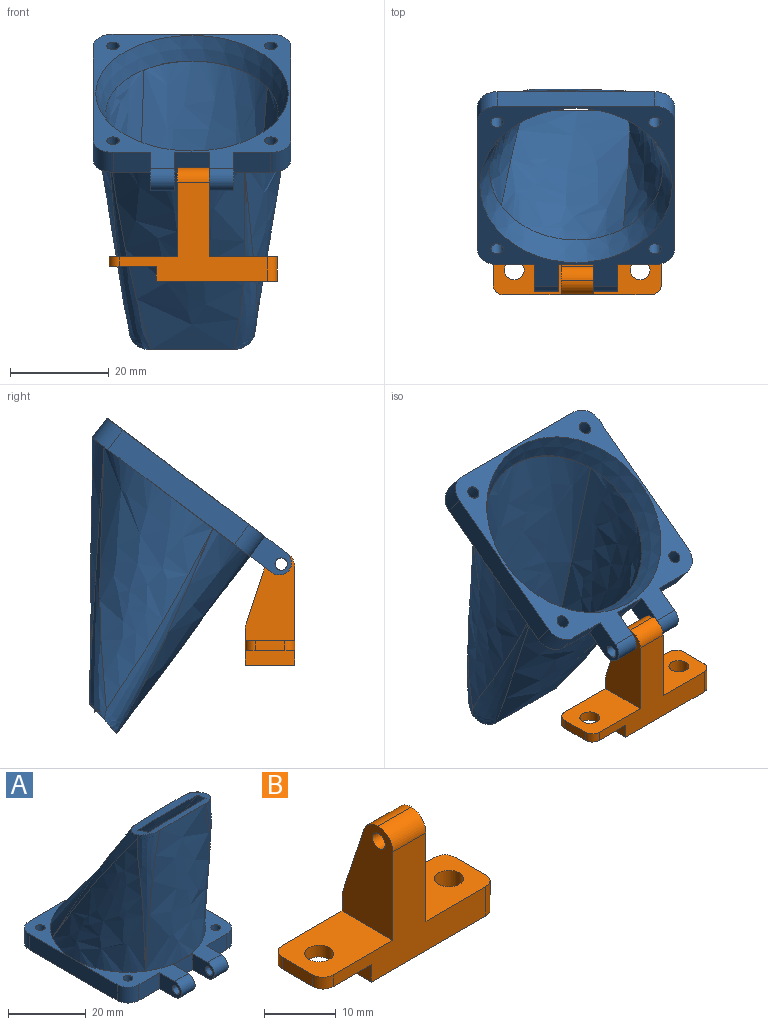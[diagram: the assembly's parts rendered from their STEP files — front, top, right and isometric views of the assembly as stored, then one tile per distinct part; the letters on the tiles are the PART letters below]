
ASSEMBLY  parts=2 mates=1
PART A: 43 faces, bbox 44.2x52x56.3 mm
  f0: plane 10.18x0.1mm, normal (0,0,1), area 0.2mm2, adj f1,f36
  f1: bspline ~45.9x29.52mm, area 1053.7mm2, adj f0,f9,f10,f32,f34,f36
  f2: bspline ~45.46x37.26mm, area 519.5mm2, adj f9,f26,f34,f35
  f3: bspline ~43.35x32.13mm, area 1261.1mm2, adj f11,f26,f33,f35,f36
  f4: bspline ~45.45x30.84mm, area 508mm2, adj f10,f11,f32,f33
  f5: offset ~49.9x34mm, area 1069.4mm2, adj f6,f8,f36,f37
  f6: offset ~50x41.44mm, area 693.2mm2, adj f5,f7,f36,f37
  f7: offset ~50.46x38.1mm, area 1281.9mm2, adj f6,f8,f36,f37
  f8: offset ~49.9x34.94mm, area 583mm2, adj f5,f7,f36,f37
  f9: plane 25.5x20mm, normal (0,0,1), area 105mm2, adj f1,f2,f12,f13,f19,f20,f24,f25
  f10: plane 25.5x20mm, normal (0,0,1), area 105mm2, adj f1,f4,f15,f16,f17,f18,f19,f22
  f11: plane 20x20mm, normal (0,0,1), area 77.5mm2, adj f3,f4,f14,f15,f23,f30
  f12: plane 7.5x5mm, normal (0,-1,0), area 37.5mm2, adj f9,f24,f27,f28
  f13: plane 32x5mm, normal (1,0,0), area 160mm2, adj f9,f26,f27,f28,f29
  f14: plane 32x5mm, normal (0,1,0), area 160mm2, adj f11,f26,f27,f29,f30
  f15: plane 32x5mm, normal (-1,0,0), area 160mm2, adj f10,f11,f27,f30,f31
  f16: plane 7.5x5mm, normal (0,-1,0), area 37.5mm2, adj f10,f17,f27,f31
  f17: plane 8x5mm, normal (-1,0,0), area 32.4mm2, adj f10,f16,f27,f40,f42
  f18: plane 8x5mm, normal (1,0,0), area 32.4mm2, adj f10,f19,f27,f40,f42
  f19: plane 7x5mm, normal (0,-1,0), area 35mm2, adj f9,f10,f18,f20,f27
  f20: plane 8x5mm, normal (-1,0,0), area 32.4mm2, adj f9,f19,f27,f39,f41
  f21: cylinder r=1.25mm len=5mm, axis (0,0,-1), area 39.3mm2, adj f26,f27
  f22: cylinder r=1.25mm len=5mm, axis (0,0,-1), area 39.3mm2, adj f10,f27
  f23: cylinder r=1.25mm len=5mm, axis (0,0,-1), area 39.3mm2, adj f11,f27
  f24: plane 8x5mm, normal (1,0,0), area 32.4mm2, adj f9,f12,f27,f39,f41
  f25: cylinder r=1.25mm len=5mm, axis (0,0,-1), area 39.3mm2, adj f9,f27
  f26: plane 20x20mm, normal (0,0,1), area 77.5mm2, adj f2,f3,f13,f14,f21,f29
  f27: plane 45.5x40mm, normal (0,0,-1), area 427mm2, adj f12,f13,f14,f15,f16,f17,f18,f19
  f28: cylinder r=4mm len=5mm, axis (0,0,1), area 31.4mm2, adj f9,f12,f13,f27
  f29: cylinder r=4mm len=5mm, axis (0,0,-1), area 31.4mm2, adj f13,f14,f26,f27
  f30: cylinder r=4mm len=5mm, axis (0,0,1), area 31.4mm2, adj f11,f14,f15,f27
  f31: cylinder r=4mm len=5mm, axis (0,0,-1), area 31.4mm2, adj f10,f15,f16,f27
  f32: bspline ~46.99x5.06mm, area 102.3mm2, adj f1,f4,f33,f36
  f33: bspline ~46.1x27.54mm, area 138.8mm2, adj f3,f4,f32,f36
  f34: bspline ~47.06x9.69mm, area 138.8mm2, adj f1,f2,f35,f36
  f35: bspline ~47.31x34.56mm, area 89.9mm2, adj f2,f3,f34,f36
  f36: bspline ~25.73x8.91mm, area 125.5mm2, adj f0,f1,f3,f5,f6,f7,f8,f32
  f37: plane 36.83x36.41mm, normal (0,0,1), area 41.8mm2, adj f5,f6,f7,f8,f38
  f38: cone r=19.5mm half-angle=21.8deg, axis (0,0,-1), area 626mm2, adj f27,f37
  f39: cylinder r=1.25mm len=5mm, axis (1,0,0), area 39.3mm2, adj f20,f24
  f40: cylinder r=1.25mm len=5mm, axis (1,0,0), area 39.3mm2, adj f17,f18
  f41: cylinder r=2.5mm len=5mm, axis (-1,0,0), area 39.3mm2, adj f9,f20,f24,f27
  f42: cylinder r=2.5mm len=5mm, axis (-1,0,0), area 39.3mm2, adj f10,f17,f18,f27
PART B: 22 faces, bbox 34x10x23 mm
  f0: plane 30x7.51mm, normal (0,1,0), area 143.8mm2, adj f3,f7,f8,f9,f10,f15,f16,f19
  f1: plane 6x2mm, normal (-1,0,0), area 12mm2, adj f3,f16,f17,f21
  f2: plane 30x20mm, normal (0,-1,0), area 225mm2, adj f3,f7,f8,f9,f10,f13,f17,f18
  f3: plane 13.75x10mm, normal (0,0,1), area 123.2mm2, adj f0,f1,f2,f5,f9,f16,f17
  f4: plane 6x5mm, normal (1,0,0), area 30mm2, adj f7,f8,f18,f19
  f5: cylinder r=2mm len=4mm, axis (0,0,1), area 25.1mm2, adj f3,f21
  f6: cylinder r=2mm len=5mm, axis (0,0,1), area 62.8mm2, adj f7,f8
  f7: plane 24.5x10mm, normal (0,0,-1), area 230.7mm2, adj f0,f2,f4,f6,f18,f19,f20
  f8: plane 13.75x10mm, normal (0,0,1), area 123.2mm2, adj f0,f2,f4,f6,f10,f18,f19
  f9: plane 18x10mm, normal (-1,0,0), area 134.8mm2, adj f0,f2,f3,f11,f12,f13,f14,f15
  f10: plane 18x10mm, normal (1,0,0), area 134.8mm2, adj f0,f2,f8,f11,f12,f13,f14,f15
  f11: cylinder r=1.25mm len=6.5mm, axis (1,0,0), area 51.1mm2, adj f9,f10
  f12: plane 12.49x6.5mm, normal (0,0.95,0.32), area 85.6mm2, adj f9,f10,f14,f15
  f13: cylinder r=3mm len=6.5mm, axis (1,0,0), area 30.1mm2, adj f2,f9,f10,f14
  f14: cylinder r=3mm len=6.5mm, axis (-1,0,0), area 23.8mm2, adj f9,f10,f12,f13
  f15: cylinder r=3mm len=6.5mm, axis (-1,0,0), area 6.3mm2, adj f0,f9,f10,f12
  f16: cylinder r=2mm len=2mm, axis (0,0,-1), area 6.3mm2, adj f0,f1,f3,f21
  f17: cylinder r=2mm len=2mm, axis (0,0,1), area 6.3mm2, adj f1,f2,f3,f21
  f18: cylinder r=2mm len=5mm, axis (0,0,-1), area 15.7mm2, adj f2,f4,f7,f8
  f19: cylinder r=2mm len=5mm, axis (0,0,1), area 15.7mm2, adj f0,f4,f7,f8
  f20: plane 10x3mm, normal (-1,0,0), area 30mm2, adj f0,f2,f7,f21
  f21: plane 10x9.5mm, normal (0,0,-1), area 80.7mm2, adj f0,f1,f2,f5,f16,f17,f20
PLACE A rot(axis=(0,-0.95,-0.32),180deg) t=(-16.88,-5.13,21.88)mm
PLACE B t=(-16.63,-1.98,3.18)mm fixed
MATE revolute B.f11 <-> A.f39  axis (1,0,0) through (-13.38,-9.23,15.68)mm
